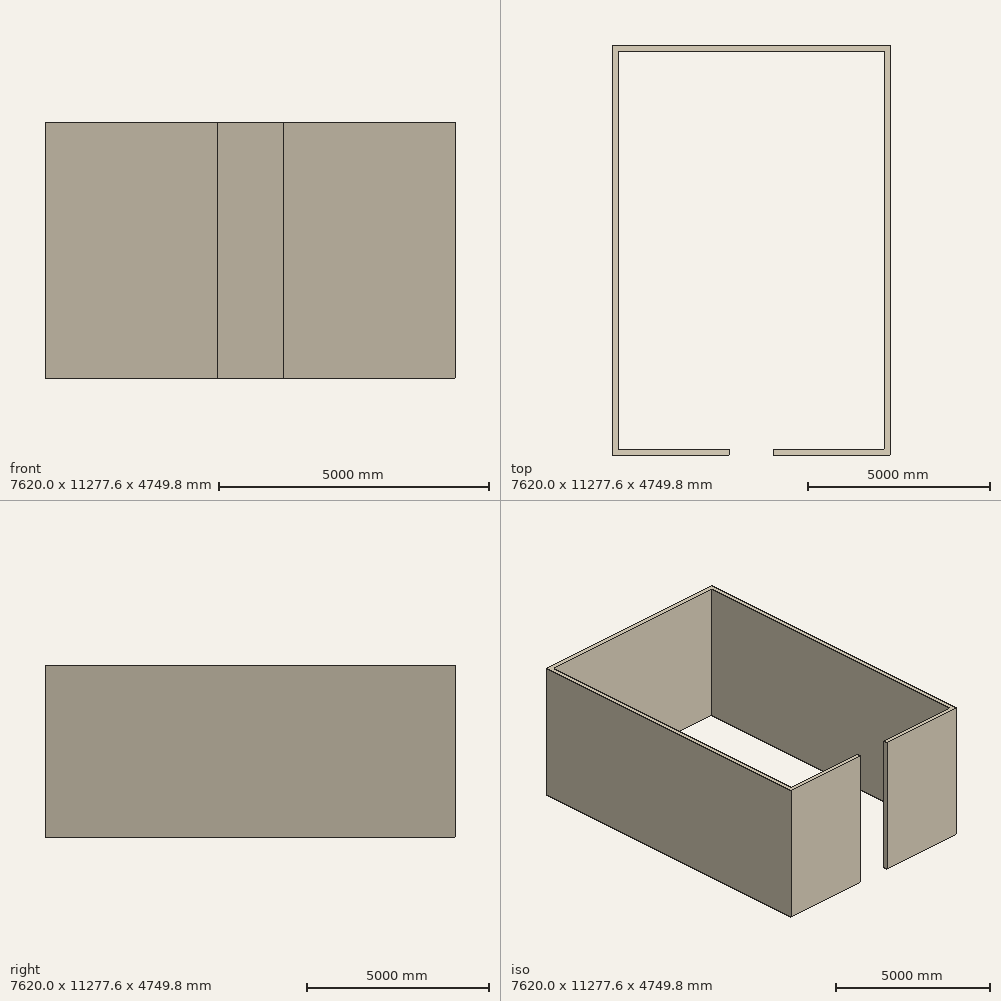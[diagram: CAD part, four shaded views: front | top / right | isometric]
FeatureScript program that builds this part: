
annotation { "Feature Type Name" : "Feature", "Feature Type Description" : "" }
export const myFeature = defineFeature(function(context is Context, id is Id, definition is map)
    precondition{}
    {
        {
            var Q0;
            Q0=qCreatedBy(makeId("Top.planeOp"),FACE);
            var sketch = newSketch(context, id + "F0", { "sketchPlane" : qUnion([Q0])});
            skLineSegment(sketch, "E0.bottom", {"start": v(3810, 5638.8) * mm, "end": v(-3810, 5638.8) * mm});
            skLineSegment(sketch, "E0.top", {"start": v(3810, -5638.8) * mm, "end": v(-3810, -5638.8) * mm});
            skLineSegment(sketch, "E0.left", {"start": v(3810, 5638.8) * mm, "end": v(3810, -5638.8) * mm});
            skLineSegment(sketch, "E0.right", {"start": v(-3810, 5638.8) * mm, "end": v(-3810, -5638.8) * mm});
            skPoint(sketch, "E0.middle", {"position": v(0, 0) * mm});
            skSolve(sketch);
        }
        {
            var Q0;
            Q0=makeQuery(id+"F0.imprint","IMPRINT",FACE,{"disambiguationData":[TD([[makeQuery(id+"F0.imprint","IMPRINT",EDGE,{"derivedFrom":sQuery(id+"F0.wireOp",EDGE,"E0.bottom")}),1.0]])]});
            extrude(context, id + "F1", {"entities" : qUnion([Q0]), "depth" : 4749.8 * mm, "offsetDistance" : 25.4 * mm});
        }
        {
            var Q0;
            Q0=makeQuery(id+"F1.opExtrude","CAP_FACE",FACE,{"disambiguationData":[OSD([sQuery(id+"F0.wireOp",EDGE,"E0.bottom"),sQuery(id+"F0.wireOp",EDGE,"E0.top"),sQuery(id+"F0.wireOp",EDGE,"E0.left"),sQuery(id+"F0.wireOp",EDGE,"E0.right")])],"isStart":false});
            var Q1;
            Q1=makeQuery(id+"F1.opExtrude","CAP_FACE",FACE,{"disambiguationData":[OSD([sQuery(id+"F0.wireOp",EDGE,"E0.bottom"),sQuery(id+"F0.wireOp",EDGE,"E0.top"),sQuery(id+"F0.wireOp",EDGE,"E0.left"),sQuery(id+"F0.wireOp",EDGE,"E0.right")])],"isStart":true});
            shell(context, id + "F2", {"entities" : qUnion([Q0, Q1]), "thickness" : 152.4 * mm});
        }
        {
            var Q0;
            Q0=makeQuery(id+"F1.opExtrude","CAP_FACE",FACE,{"disambiguationData":[OSD([sQuery(id+"F0.wireOp",EDGE,"E0.bottom"),sQuery(id+"F0.wireOp",EDGE,"E0.top"),sQuery(id+"F0.wireOp",EDGE,"E0.left"),sQuery(id+"F0.wireOp",EDGE,"E0.right")])],"isStart":false});
            var sketch = newSketch(context, id + "F3", { "sketchPlane" : qUnion([Q0])});
            skPoint(sketch, "E1", {"position": v(0, -5562.6) * mm});
            skLineSegment(sketch, "E2.bottom", {"start": v(609.6, -5486.4) * mm, "end": v(-609.6, -5486.4) * mm});
            skLineSegment(sketch, "E2.top", {"start": v(609.6, -5638.8) * mm, "end": v(-609.6, -5638.8) * mm});
            skLineSegment(sketch, "E2.left", {"start": v(609.6, -5486.4) * mm, "end": v(609.6, -5638.8) * mm});
            skLineSegment(sketch, "E2.right", {"start": v(-609.6, -5486.4) * mm, "end": v(-609.6, -5638.8) * mm});
            skSolve(sketch);
        }
        {
            var Q0;
            Q0=makeQuery(id+"F3.imprint","IMPRINT",FACE,{"disambiguationData":[TD([[makeQuery(id+"F3.imprint","IMPRINT",EDGE,{"derivedFrom":sQuery(id+"F3.wireOp",EDGE,"E2.bottom")}),1.0]])]});
            extrude(context, id + "F4", {"entities" : qUnion([Q0]), "operationType" : NewBodyOperationType.REMOVE, "oppositeDirection" : true, "depth" : 4749.8 * mm, "offsetDistance" : 25.4 * mm});
        }
    });
